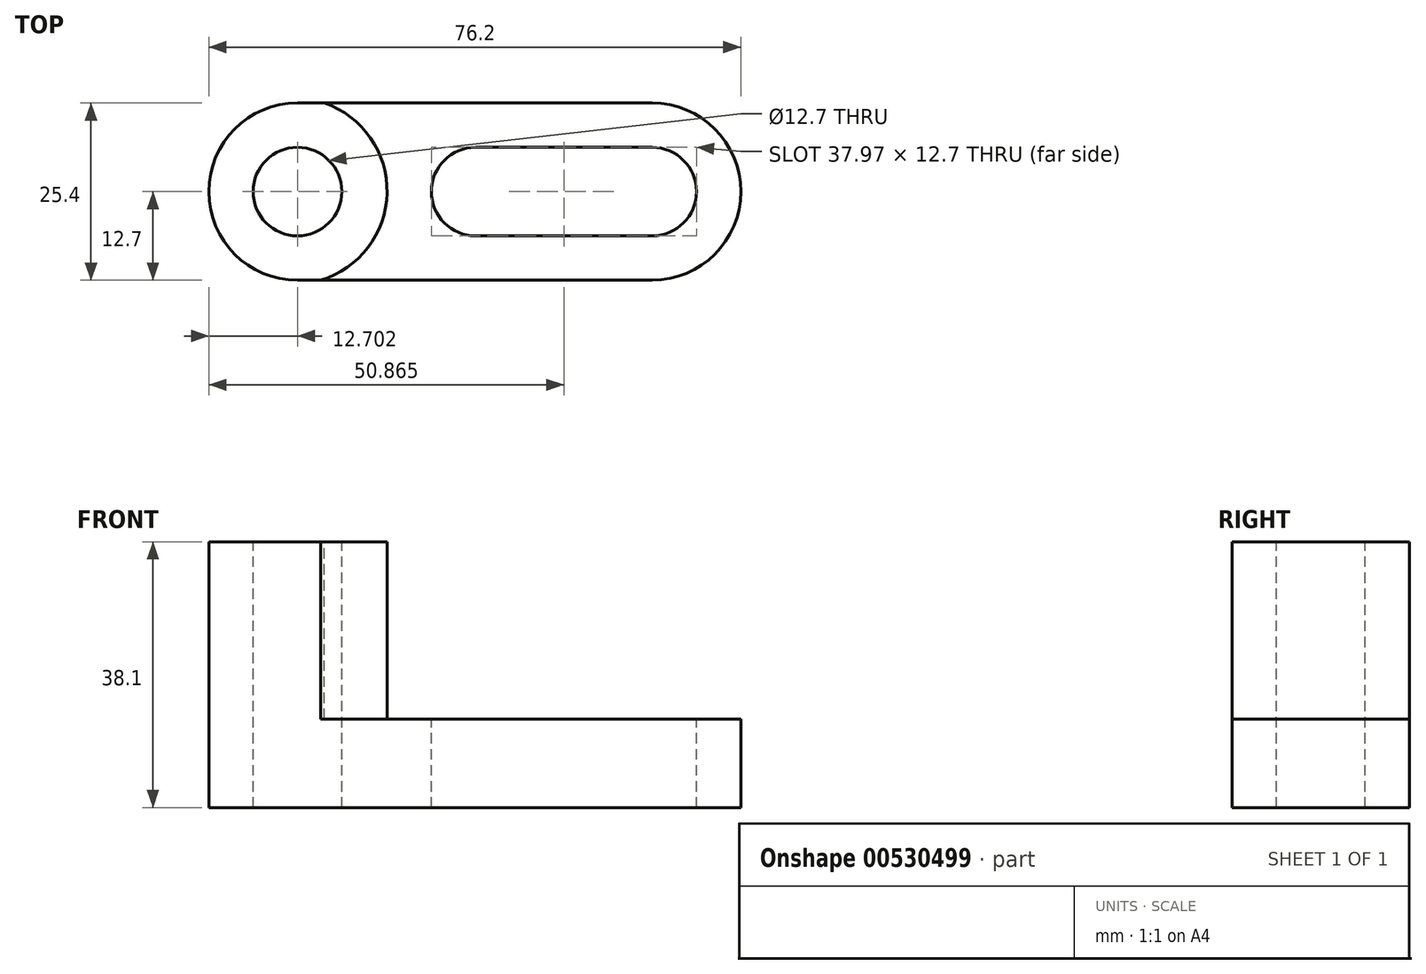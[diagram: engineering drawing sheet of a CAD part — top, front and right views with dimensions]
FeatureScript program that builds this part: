
annotation { "Feature Type Name" : "Feature", "Feature Type Description" : "" }
export const myFeature = defineFeature(function(context is Context, id is Id, definition is map)
    precondition{}
    {
        {
            var Q0;
            Q0=qCreatedBy(makeId("Front.planeOp"),FACE);
            var sketch = newSketch(context, id + "F0", { "sketchPlane" : qUnion([Q0])});
            skLineSegment(sketch, "E0", {"start": v(-54.16, 38.1) * mm, "end": v(-54.16, 0) * mm});
            skLineSegment(sketch, "E1", {"start": v(-54.16, 0) * mm, "end": v(22.04, 0) * mm});
            skLineSegment(sketch, "E2", {"start": v(22.04, 0) * mm, "end": v(22.04, 12.7) * mm});
            skLineSegment(sketch, "E3", {"start": v(22.04, 12.7) * mm, "end": v(-28.76, 12.7) * mm});
            skLineSegment(sketch, "E4", {"start": v(-28.76, 12.7) * mm, "end": v(-28.76, 38.1) * mm});
            skLineSegment(sketch, "E5", {"start": v(-28.76, 38.1) * mm, "end": v(-54.16, 38.1) * mm});
            skSolve(sketch);
        }
        {
            var Q0;
            Q0 = qSketchRegion(id + "F0", true);
            extrude(context, id + "F1", {"entities" : qUnion([Q0]), "depth" : 25.4 * mm, "offsetDistance" : 25.4 * mm});
        }
        {
            var Q0;
            Q0=makeQuery(id+"F1.opExtrude","SWEPT_FACE",FACE,{"disambiguationData":[OSD([sQuery(id+"F0.wireOp",EDGE,"E3")])]});
            var sketch = newSketch(context, id + "F2", { "sketchPlane" : qUnion([Q0])});
            skArc(sketch, "E6", {"start": v(-28.76, -25.4) * mm, "mid": v(-23.82, -12.7) * mm, "end": v(-28.76, 0) * mm});
            skLineSegment(sketch, "E7", {"start": v(-28.76, 0) * mm, "end": v(-28.76, -25.4) * mm});
            skSolve(sketch);
        }
        {
            var Q0;
            Q0 = qSketchRegion(id + "F2", true);
            extrude(context, id + "F3", {"entities" : qUnion([Q0]), "operationType" : NewBodyOperationType.ADD, "depth" : 25.4 * mm, "offsetDistance" : 25.4 * mm});
        }
        {
            var Q0;
            Q0=makeQuery(id+"F3.boolean.opBoolean","MERGE",FACE,{"derivedFrom":[makeQuery(id+"F1.opExtrude","SWEPT_FACE",FACE,{"disambiguationData":[OSD([sQuery(id+"F0.wireOp",EDGE,"E5")])]}),makeQuery(id+"F3.opExtrude","CAP_FACE",FACE,{"disambiguationData":[OSD([sQuery(id+"F2.wireOp",EDGE,"E6"),sQuery(id+"F2.wireOp",EDGE,"E7")])],"isStart":false})]});
            var sketch = newSketch(context, id + "F4", { "sketchPlane" : qUnion([Q0])});
            skCircle(sketch, "E8", {"center": v(-41.46, -12.7) * mm, "radius": 6.35 * mm});
            skPoint(sketch, "E8.centerSnap0", {"position": v(-23.82, -12.7) * mm});
            skCircle(sketch, "E9", {"center": v(-41.46, -12.7) * mm, "radius": 12.7 * mm});
            skSolve(sketch);
        }
        {
            var Q0;
            {var subQ0=sQuery(id+"F4.wireOp",EDGE,"E9");var subQ1=sQuery(id+"F0.wireOp",EDGE,"E5");var subQ4=makeQuery(id+"F1.opExtrude","CAP_EDGE",EDGE,{"disambiguationData":[OSD([subQ1])],"isStart":true});var subQ5=makeQuery(id+"F4.imprint","INTERSECT",VERTEX,{"derivedFrom":[subQ4,subQ0]});Q0=makeQuery(id+"F4.imprint","IMPRINT",FACE,{"disambiguationData":[TD([[makeQuery(id+"F4.imprint","IMPRINT",EDGE,{"disambiguationData":[TD([[subQ5,-1.0]])],"derivedFrom":subQ0}),-1.0]])]});}
            var Q1;
            {var subQ0=sQuery(id+"F4.wireOp",EDGE,"E9");var subQ1=sQuery(id+"F0.wireOp",EDGE,"E5");var subQ4=makeQuery(id+"F1.opExtrude","CAP_EDGE",EDGE,{"disambiguationData":[OSD([subQ1])],"isStart":false});var subQ5=makeQuery(id+"F4.imprint","INTERSECT",VERTEX,{"derivedFrom":[subQ4,subQ0]});Q1=makeQuery(id+"F4.imprint","IMPRINT",FACE,{"disambiguationData":[TD([[makeQuery(id+"F4.imprint","IMPRINT",EDGE,{"disambiguationData":[TD([[subQ5,1.0]])],"derivedFrom":subQ0}),-1.0]])]});}
            var Q2;
            Q2=makeQuery(id+"F4.imprint","IMPRINT",FACE,{"disambiguationData":[TD([[makeQuery(id+"F4.imprint","IMPRINT",EDGE,{"derivedFrom":sQuery(id+"F4.wireOp",EDGE,"E8")}),1.0]])]});
            extrude(context, id + "F5", {"entities" : qUnion([Q0, Q1, Q2]), "operationType" : NewBodyOperationType.REMOVE, "oppositeDirection" : true, "depth" : 127 * mm, "offsetDistance" : 25.4 * mm});
        }
        {
            var Q0;
            Q0=makeQuery(id+"F3.boolean.opBoolean","MERGE",FACE,{"derivedFrom":[makeQuery(id+"F1.opExtrude","SWEPT_FACE",FACE,{"disambiguationData":[OSD([sQuery(id+"F0.wireOp",EDGE,"E5")])]}),makeQuery(id+"F3.opExtrude","CAP_FACE",FACE,{"disambiguationData":[OSD([sQuery(id+"F2.wireOp",EDGE,"E6"),sQuery(id+"F2.wireOp",EDGE,"E7")])],"isStart":false})]});
            var sketch = newSketch(context, id + "F6", { "sketchPlane" : qUnion([Q0])});
            skArc(sketch, "E10", {"start": v(-38.16, -25.4) * mm, "mid": v(-28.63, -12.9) * mm, "end": v(-37.6, 0) * mm});
            skSolve(sketch);
        }
        {
            var Q0;
            Q0 = qSketchRegion(id + "F6", true);
            var Q1;
            {var subQ0=sQuery(id+"F6.wireOp",EDGE,"E10");Q1=makeQuery(id+"F6.imprint","IMPRINT",FACE,{"disambiguationData":[TD([[makeQuery(id+"F6.imprint","IMPRINT",EDGE,{"derivedFrom":subQ0}),-1.0]])]});}
            extrude(context, id + "F7", {"entities" : qUnion([Q0, Q1]), "operationType" : NewBodyOperationType.REMOVE, "oppositeDirection" : true, "depth" : 25.4 * mm, "offsetDistance" : 25.4 * mm});
        }
        {
            var Q0;
            Q0=makeQuery(id+"F7.boolean.opBoolean","MERGE",FACE,{"derivedFrom":[makeQuery(id+"F1.opExtrude","SWEPT_FACE",FACE,{"disambiguationData":[OSD([sQuery(id+"F0.wireOp",EDGE,"E3")])]}),makeQuery(id+"F7.opExtrude","CAP_FACE",FACE,{"disambiguationData":[OSD([sQuery(id+"F0.wireOp",EDGE,"E5"),sQuery(id+"F2.wireOp",EDGE,"E6"),sQuery(id+"F6.wireOp",EDGE,"E10")])],"isStart":false})]});
            var sketch = newSketch(context, id + "F8", { "sketchPlane" : qUnion([Q0])});
            skCircle(sketch, "E11", {"center": v(-15.93, -12.7) * mm, "radius": 6.35 * mm});
            skCircle(sketch, "E12", {"center": v(9.34, -12.7) * mm, "radius": 6.35 * mm});
            skLineSegment(sketch, "E13", {"start": v(9.34, -6.35) * mm, "end": v(-15.93, -6.35) * mm});
            skLineSegment(sketch, "E14", {"start": v(-15.93, -19.05) * mm, "end": v(9.34, -19.05) * mm});
            skLineSegment(sketch, "E15", {"start": v(9.34, 0) * mm, "end": v(8.62, -1.87) * mm});
            skArc(sketch, "E16", {"start": v(9.34, -25.4) * mm, "mid": v(22.04, -12.7) * mm, "end": v(9.34, 0) * mm});
            skSolve(sketch);
        }
        {
            var Q0;
            {var subQ0=sQuery(id+"F8.wireOp",EDGE,"E12");var subQ1=makeQuery(id+"F8.imprint","INTERSECT",VERTEX,{"derivedFrom":[subQ0,sQuery(id+"F8.wireOp",EDGE,"E13")]});Q0=makeQuery(id+"F8.imprint","IMPRINT",FACE,{"disambiguationData":[TD([[makeQuery(id+"F8.imprint","IMPRINT",EDGE,{"disambiguationData":[TD([[subQ1,-1.0]])],"derivedFrom":subQ0}),1.0]])]});}
            var Q1;
            {var subQ0=sQuery(id+"F8.wireOp",EDGE,"E13");Q1=makeQuery(id+"F8.imprint","IMPRINT",FACE,{"disambiguationData":[TD([[makeQuery(id+"F8.imprint","IMPRINT",EDGE,{"derivedFrom":subQ0}),1.0]])]});}
            var Q2;
            {var subQ0=sQuery(id+"F8.wireOp",EDGE,"E11");var subQ1=makeQuery(id+"F8.imprint","INTERSECT",VERTEX,{"derivedFrom":[subQ0,sQuery(id+"F8.wireOp",EDGE,"E13")]});Q2=makeQuery(id+"F8.imprint","IMPRINT",FACE,{"disambiguationData":[TD([[makeQuery(id+"F8.imprint","IMPRINT",EDGE,{"disambiguationData":[TD([[subQ1,-1.0]])],"derivedFrom":subQ0}),1.0]])]});}
            var Q3;
            {var subQ0=sQuery(id+"F8.wireOp",EDGE,"MQ9r8B5C-AfsR-uiwF-66Vf-lGnayfBOl7iR");var subQ3=sQuery(id+"F0.wireOp",EDGE,"E3");var subQ6=makeQuery(id+"F1.opExtrude","SWEPT_EDGE",EDGE,{"disambiguationData":[OSD([sQuery(id+"F0.wireOp",EDGE,"E2"),subQ3])]});var subQ7=makeQuery(id+"F8.imprint","INTERSECT",VERTEX,{"derivedFrom":[subQ6,subQ0]});Q3=makeQuery(id+"F8.imprint","IMPRINT",FACE,{"disambiguationData":[TD([[makeQuery(id+"F8.imprint","IMPRINT",EDGE,{"disambiguationData":[TD([[subQ7,-1.0]])],"derivedFrom":subQ0}),-1.0]])]});}
            var Q4;
            {var subQ0=sQuery(id+"F8.wireOp",EDGE,"MQ9r8B5C-AfsR-uiwF-66Vf-lGnayfBOl7iR");var subQ3=sQuery(id+"F0.wireOp",EDGE,"E3");var subQ6=makeQuery(id+"F1.opExtrude","SWEPT_EDGE",EDGE,{"disambiguationData":[OSD([sQuery(id+"F0.wireOp",EDGE,"E2"),subQ3])]});var subQ7=makeQuery(id+"F8.imprint","INTERSECT",VERTEX,{"derivedFrom":[subQ6,subQ0]});Q4=makeQuery(id+"F8.imprint","IMPRINT",FACE,{"disambiguationData":[TD([[makeQuery(id+"F8.imprint","IMPRINT",EDGE,{"disambiguationData":[TD([[subQ7,1.0]])],"derivedFrom":subQ0}),-1.0]])]});}
            var Q5;
            {var subQ0=sQuery(id+"F8.wireOp",EDGE,"E16");var subQ3=sQuery(id+"F0.wireOp",EDGE,"E3");var subQ6=makeQuery(id+"F1.opExtrude","SWEPT_EDGE",EDGE,{"disambiguationData":[OSD([sQuery(id+"F0.wireOp",EDGE,"E2"),subQ3])]});var subQ7=makeQuery(id+"F8.imprint","INTERSECT",VERTEX,{"derivedFrom":[subQ6,subQ0]});Q5=makeQuery(id+"F8.imprint","IMPRINT",FACE,{"disambiguationData":[TD([[makeQuery(id+"F8.imprint","IMPRINT",EDGE,{"disambiguationData":[TD([[subQ7,-1.0]])],"derivedFrom":subQ0}),-1.0]])]});}
            var Q6;
            {var subQ0=sQuery(id+"F8.wireOp",EDGE,"E16");var subQ3=sQuery(id+"F0.wireOp",EDGE,"E3");var subQ6=makeQuery(id+"F1.opExtrude","SWEPT_EDGE",EDGE,{"disambiguationData":[OSD([sQuery(id+"F0.wireOp",EDGE,"E2"),subQ3])]});var subQ7=makeQuery(id+"F8.imprint","INTERSECT",VERTEX,{"derivedFrom":[subQ6,subQ0]});Q6=makeQuery(id+"F8.imprint","IMPRINT",FACE,{"disambiguationData":[TD([[makeQuery(id+"F8.imprint","IMPRINT",EDGE,{"disambiguationData":[TD([[subQ7,1.0]])],"derivedFrom":subQ0}),-1.0]])]});}
            extrude(context, id + "F9", {"entities" : qUnion([Q0, Q1, Q2, Q3, Q4, Q5, Q6]), "operationType" : NewBodyOperationType.REMOVE, "oppositeDirection" : true, "depth" : 25.4 * mm, "offsetDistance" : 25.4 * mm});
        }
    });
